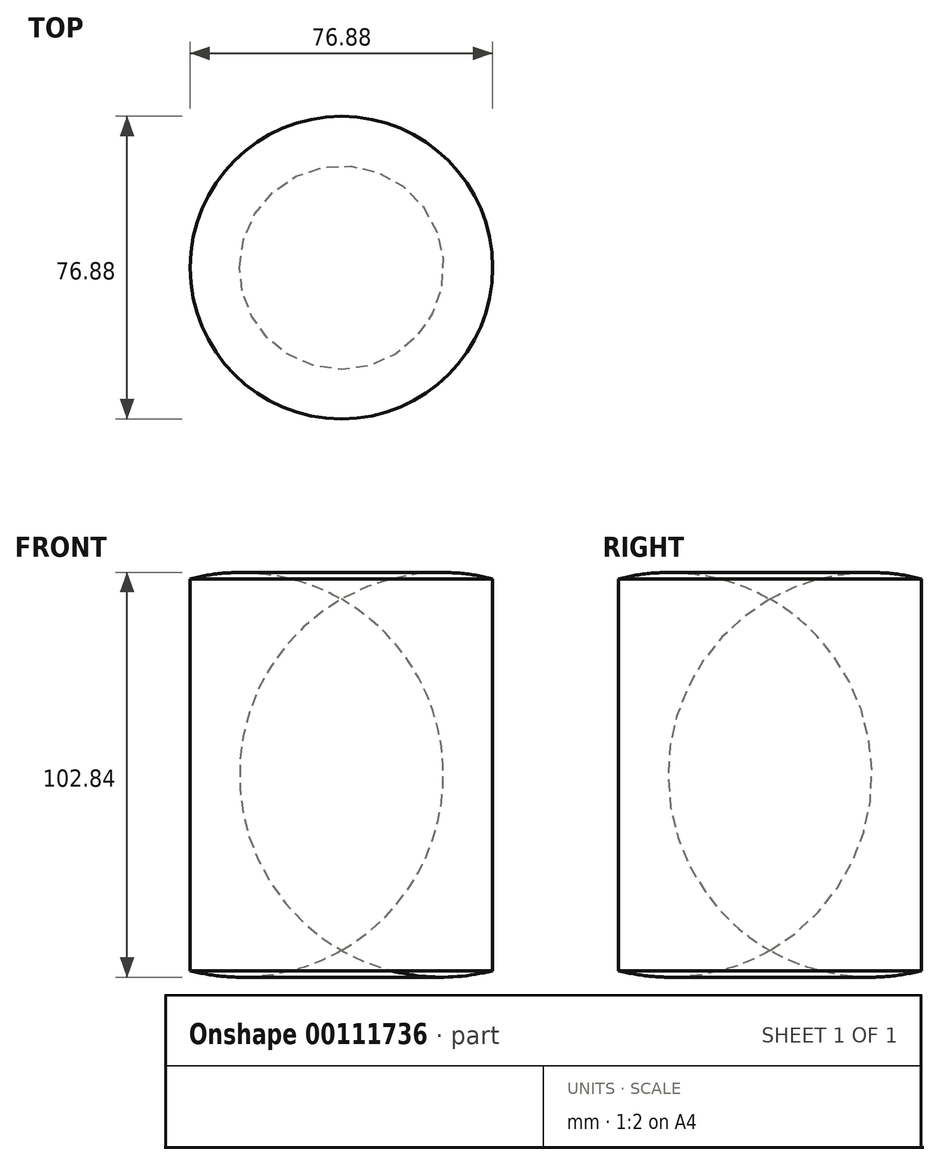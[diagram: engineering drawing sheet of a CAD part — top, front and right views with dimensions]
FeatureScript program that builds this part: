
annotation { "Feature Type Name" : "Feature", "Feature Type Description" : "" }
export const myFeature = defineFeature(function(context is Context, id is Id, definition is map)
    precondition{}
    {
        {
            var Q0;
            Q0=qCreatedBy(makeId("Front.planeOp"),FACE);
            var sketch = newSketch(context, id + "F0", { "sketchPlane" : qUnion([Q0])});
            skLineSegment(sketch, "E0", {"start": v(-63.17, 55.28) * mm, "end": v(-63.17, -43.66) * mm});
            skLineSegment(sketch, "E1", {"start": v(-24.73, 55.87) * mm, "end": v(-24.73, -43.66) * mm});
            skArc(sketch, "E2", {"start": v(-24.73, -43.66) * mm, "mid": v(13.75, 6.1) * mm, "end": v(-24.73, 55.87) * mm});
            skSolve(sketch);
        }
        {
            var Q0;
            Q0=makeQuery(id+"F0.imprint","IMPRINT",FACE,{"disambiguationData":[TD([[makeQuery(id+"F0.imprint","IMPRINT",EDGE,{"derivedFrom":sQuery(id+"F0.wireOp",EDGE,"E1")}),1.0]])]});
            var Q1;
            Q1=sQuery(id+"F0.wireOp",EDGE,"E0");
            revolve(context, id + "F1", {"entities" : qUnion([Q0]), "axis" : qUnion([Q1]), "revolveType" : RevolveType.FULL});
        }
    });
